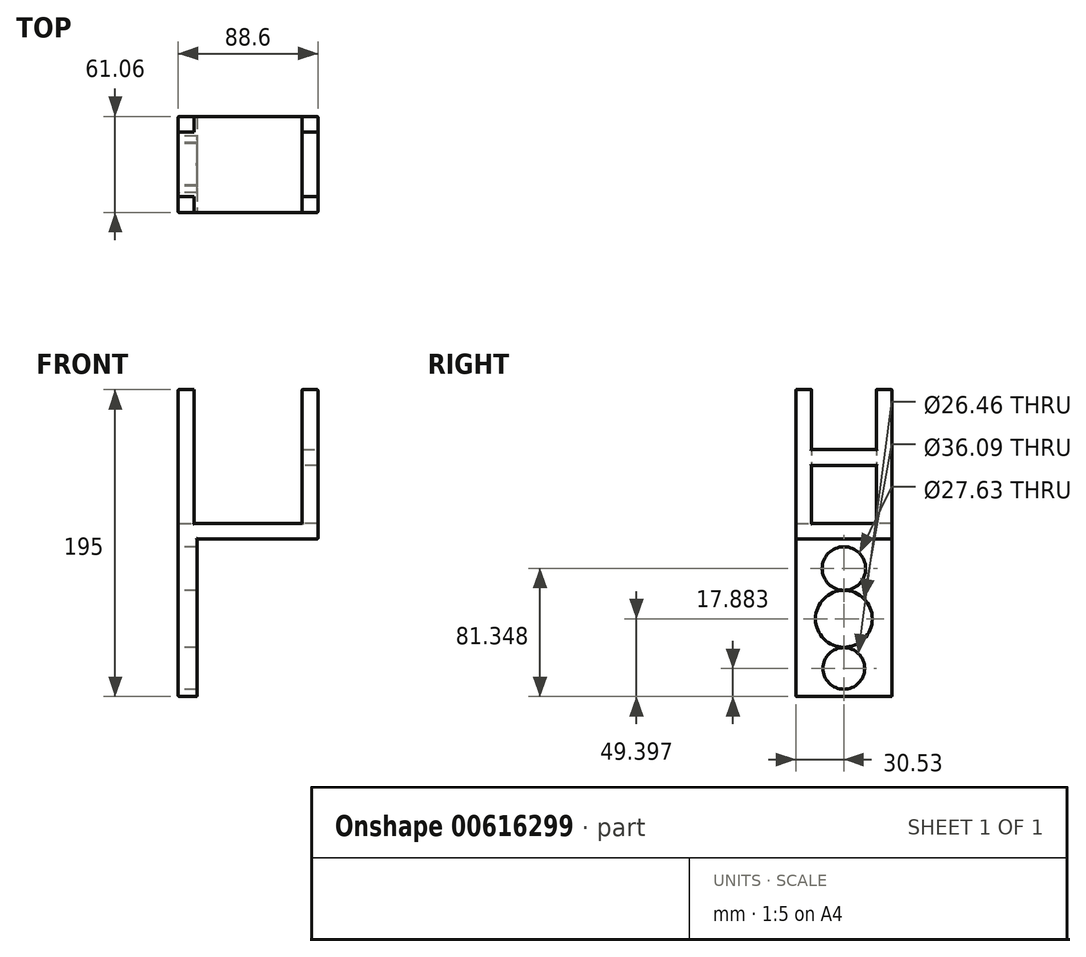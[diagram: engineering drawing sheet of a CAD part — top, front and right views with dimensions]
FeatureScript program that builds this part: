
annotation { "Feature Type Name" : "Feature", "Feature Type Description" : "" }
export const myFeature = defineFeature(function(context is Context, id is Id, definition is map)
    precondition{}
    {
        {
            var Q0;
            Q0=qCreatedBy(makeId("Top.planeOp"),FACE);
            var sketch = newSketch(context, id + "F0", { "sketchPlane" : qUnion([Q0])});
            skLineSegment(sketch, "E0.bottom", {"start": v(44.3, -30.53) * mm, "end": v(-44.3, -30.53) * mm});
            skLineSegment(sketch, "E0.top", {"start": v(44.3, 30.53) * mm, "end": v(-44.3, 30.53) * mm});
            skLineSegment(sketch, "E0.left", {"start": v(44.3, -30.53) * mm, "end": v(44.3, 30.53) * mm});
            skLineSegment(sketch, "E0.right", {"start": v(-44.3, -30.53) * mm, "end": v(-44.3, 30.53) * mm});
            skPoint(sketch, "E0.middle", {"position": v(0, 0) * mm});
            skSolve(sketch);
        }
        {
            var Q0;
            Q0=makeQuery(id+"F0.imprint","IMPRINT",FACE,{"disambiguationData":[TD([[makeQuery(id+"F0.imprint","IMPRINT",EDGE,{"derivedFrom":sQuery(id+"F0.wireOp",EDGE,"E0.bottom")}),-1.0]])]});
            extrude(context, id + "F1", {"entities" : qUnion([Q0]), "depth" : 10 * mm, "offsetDistance" : 25.4 * mm});
        }
        {
            var Q0;
            Q0=makeQuery(id+"F1.opExtrude","CAP_FACE",FACE,{"disambiguationData":[OSD([sQuery(id+"F0.wireOp",EDGE,"E0.bottom"),sQuery(id+"F0.wireOp",EDGE,"E0.top"),sQuery(id+"F0.wireOp",EDGE,"E0.left"),sQuery(id+"F0.wireOp",EDGE,"E0.right")])],"isStart":false});
            var sketch = newSketch(context, id + "F2", { "sketchPlane" : qUnion([Q0])});
            skLineSegment(sketch, "E1.bottom", {"start": v(-44.3, 30.53) * mm, "end": v(-34.3, 30.53) * mm});
            skLineSegment(sketch, "E1.top", {"start": v(-44.3, 20.53) * mm, "end": v(-34.3, 20.53) * mm});
            skLineSegment(sketch, "E1.left", {"start": v(-44.3, 30.53) * mm, "end": v(-44.3, 20.53) * mm});
            skLineSegment(sketch, "E1.right", {"start": v(-34.3, 30.53) * mm, "end": v(-34.3, 20.53) * mm});
            skLineSegment(sketch, "E2.bottom", {"start": v(44.3, 30.53) * mm, "end": v(34.3, 30.53) * mm});
            skLineSegment(sketch, "E2.top", {"start": v(44.3, 20.53) * mm, "end": v(34.3, 20.53) * mm});
            skLineSegment(sketch, "E2.left", {"start": v(44.3, 30.53) * mm, "end": v(44.3, 20.53) * mm});
            skLineSegment(sketch, "E2.right", {"start": v(34.3, 30.53) * mm, "end": v(34.3, 20.53) * mm});
            skLineSegment(sketch, "E3.bottom", {"start": v(44.3, -30.53) * mm, "end": v(34.3, -30.53) * mm});
            skLineSegment(sketch, "E3.top", {"start": v(44.3, -20.53) * mm, "end": v(34.3, -20.53) * mm});
            skLineSegment(sketch, "E3.left", {"start": v(44.3, -30.53) * mm, "end": v(44.3, -20.53) * mm});
            skLineSegment(sketch, "E3.right", {"start": v(34.3, -30.53) * mm, "end": v(34.3, -20.53) * mm});
            skLineSegment(sketch, "E4.bottom", {"start": v(-44.3, -30.53) * mm, "end": v(-34.3, -30.53) * mm});
            skLineSegment(sketch, "E4.top", {"start": v(-44.3, -20.53) * mm, "end": v(-34.3, -20.53) * mm});
            skLineSegment(sketch, "E4.left", {"start": v(-44.3, -30.53) * mm, "end": v(-44.3, -20.53) * mm});
            skLineSegment(sketch, "E4.right", {"start": v(-34.3, -30.53) * mm, "end": v(-34.3, -20.53) * mm});
            skSolve(sketch);
        }
        {
            var Q0;
            Q0=makeQuery(id+"F2.imprint","IMPRINT",FACE,{"disambiguationData":[TD([[makeQuery(id+"F2.imprint","IMPRINT",EDGE,{"derivedFrom":sQuery(id+"F2.wireOp",EDGE,"E1.bottom")}),1.0]])]});
            var Q1;
            Q1=makeQuery(id+"F2.imprint","IMPRINT",FACE,{"disambiguationData":[TD([[makeQuery(id+"F2.imprint","IMPRINT",EDGE,{"derivedFrom":sQuery(id+"F2.wireOp",EDGE,"E2.bottom")}),1.0]])]});
            var Q2;
            Q2=makeQuery(id+"F2.imprint","IMPRINT",FACE,{"disambiguationData":[TD([[makeQuery(id+"F2.imprint","IMPRINT",EDGE,{"derivedFrom":sQuery(id+"F2.wireOp",EDGE,"E3.bottom")}),-1.0]])]});
            var Q3;
            Q3=makeQuery(id+"F2.imprint","IMPRINT",FACE,{"disambiguationData":[TD([[makeQuery(id+"F2.imprint","IMPRINT",EDGE,{"derivedFrom":sQuery(id+"F2.wireOp",EDGE,"E4.bottom")}),-1.0]])]});
            extrude(context, id + "F3", {"entities" : qUnion([Q0, Q1, Q2, Q3]), "operationType" : NewBodyOperationType.ADD, "depth" : 85 * mm, "offsetDistance" : 25 * mm});
        }
        {
            var Q0;
            Q0=makeQuery(id+"F1.opExtrude","CAP_FACE",FACE,{"disambiguationData":[OSD([sQuery(id+"F0.wireOp",EDGE,"E0.bottom"),sQuery(id+"F0.wireOp",EDGE,"E0.top"),sQuery(id+"F0.wireOp",EDGE,"E0.left"),sQuery(id+"F0.wireOp",EDGE,"E0.right")])],"isStart":true});
            var sketch = newSketch(context, id + "F4", { "sketchPlane" : qUnion([Q0])});
            skLineSegment(sketch, "E5.bottom", {"start": v(-44.3, -30.53) * mm, "end": v(-32.3, -30.53) * mm});
            skLineSegment(sketch, "E5.top", {"start": v(-44.3, 30.53) * mm, "end": v(-32.3, 30.53) * mm});
            skLineSegment(sketch, "E5.left", {"start": v(-44.3, -30.53) * mm, "end": v(-44.3, 30.53) * mm});
            skLineSegment(sketch, "E5.right", {"start": v(-32.3, -30.53) * mm, "end": v(-32.3, 30.53) * mm});
            skSolve(sketch);
        }
        {
            var Q0;
            Q0=makeQuery(id+"F4.imprint","IMPRINT",FACE,{"disambiguationData":[TD([[makeQuery(id+"F4.imprint","IMPRINT",EDGE,{"derivedFrom":sQuery(id+"F4.wireOp",EDGE,"E5.bottom")}),-1.0]])]});
            extrude(context, id + "F5", {"entities" : qUnion([Q0]), "operationType" : NewBodyOperationType.ADD, "depth" : 50 * mm, "offsetDistance" : 25 * mm});
        }
        {
            var Q0;
            Q0=makeQuery(id+"F5.opExtrude","CAP_FACE",FACE,{"disambiguationData":[OSD([sQuery(id+"F4.wireOp",EDGE,"E5.bottom"),sQuery(id+"F4.wireOp",EDGE,"E5.top"),sQuery(id+"F4.wireOp",EDGE,"E5.left"),sQuery(id+"F4.wireOp",EDGE,"E5.right")])],"isStart":false});
            extrude(context, id + "F6", {"entities" : qUnion([Q0]), "operationType" : NewBodyOperationType.ADD, "depth" : 50 * mm, "offsetDistance" : 25 * mm});
        }
        {
            var Q0;
            Q0=makeQuery(id+"F3.opExtrude","SWEPT_FACE",FACE,{"disambiguationData":[OSD([sQuery(id+"F2.wireOp",EDGE,"E2.top")])]});
            var sketch = newSketch(context, id + "F7", { "sketchPlane" : qUnion([Q0])});
            skLineSegment(sketch, "E6.bottom", {"start": v(34.3, 46.8) * mm, "end": v(44.3, 46.8) * mm});
            skLineSegment(sketch, "E6.top", {"start": v(34.3, 56.89) * mm, "end": v(44.3, 56.89) * mm});
            skLineSegment(sketch, "E6.left", {"start": v(34.3, 46.8) * mm, "end": v(34.3, 56.89) * mm});
            skLineSegment(sketch, "E6.right", {"start": v(44.3, 46.8) * mm, "end": v(44.3, 56.89) * mm});
            skSolve(sketch);
        }
        {
            var Q0;
            Q0=makeQuery(id+"F7.imprint","IMPRINT",FACE,{"disambiguationData":[TD([[makeQuery(id+"F7.imprint","IMPRINT",EDGE,{"derivedFrom":sQuery(id+"F7.wireOp",EDGE,"E6.bottom")}),1.0]])]});
            extrude(context, id + "F8", {"entities" : qUnion([Q0]), "operationType" : NewBodyOperationType.ADD, "depth" : 42 * mm, "offsetDistance" : 25 * mm});
        }
        {
            var Q0;
            {var subQ0=sQuery(id+"F4.wireOp",EDGE,"E5.left");Q0=makeQuery(id+"F6.boolean.opBoolean","MERGE",FACE,{"derivedFrom":[makeQuery(id+"F5.boolean.opBoolean","MERGE",FACE,{"derivedFrom":[makeQuery(id+"F3.boolean.opBoolean","MERGE",FACE,{"derivedFrom":[makeQuery(id+"F1.opExtrude","SWEPT_FACE",FACE,{"disambiguationData":[OSD([sQuery(id+"F0.wireOp",EDGE,"E0.right")])]}),makeQuery(id+"F3.opExtrude","SWEPT_FACE",FACE,{"disambiguationData":[OSD([sQuery(id+"F2.wireOp",EDGE,"E1.left")])]}),makeQuery(id+"F3.opExtrude","SWEPT_FACE",FACE,{"disambiguationData":[OSD([sQuery(id+"F2.wireOp",EDGE,"E4.left")])]})]}),makeQuery(id+"F5.opExtrude","SWEPT_FACE",FACE,{"disambiguationData":[OSD([subQ0])]})]}),makeQuery(id+"F6.opExtrude","SWEPT_FACE",FACE,{"disambiguationData":[OSD([subQ0])]})]});}
            var sketch = newSketch(context, id + "F9", { "sketchPlane" : qUnion([Q0])});
            skCircle(sketch, "E7", {"center": v(0, -50.6) * mm, "radius": 18.04 * mm});
            skCircle(sketch, "E8", {"center": v(0, -18.65) * mm, "radius": 13.82 * mm});
            skSolve(sketch);
        }
        {
            var Q0;
            Q0=makeQuery(id+"F9.imprint","IMPRINT",FACE,{"disambiguationData":[TD([[makeQuery(id+"F9.imprint","IMPRINT",EDGE,{"derivedFrom":sQuery(id+"F9.wireOp",EDGE,"E7")}),-1.0]])]});
            var sketch = newSketch(context, id + "F10", { "sketchPlane" : qUnion([Q0])});
            skCircle(sketch, "E9", {"center": v(0, -82.12) * mm, "radius": 13.23 * mm});
            skSolve(sketch);
        }
        {
            var Q0;
            Q0=makeQuery(id+"F10.imprint","IMPRINT",FACE,{"disambiguationData":[TD([[makeQuery(id+"F10.imprint","IMPRINT",EDGE,{"derivedFrom":sQuery(id+"F10.wireOp",EDGE,"E9")}),1.0]])]});
            extrude(context, id + "F11", {"entities" : qUnion([Q0]), "operationType" : NewBodyOperationType.REMOVE, "oppositeDirection" : true, "depth" : 25 * mm, "offsetDistance" : 25 * mm});
        }
        {
            var Q0;
            Q0=makeQuery(id+"F9.imprint","IMPRINT",FACE,{"disambiguationData":[TD([[makeQuery(id+"F9.imprint","IMPRINT",EDGE,{"derivedFrom":sQuery(id+"F9.wireOp",EDGE,"E8")}),1.0]])]});
            var Q1;
            Q1=makeQuery(id+"F9.imprint","IMPRINT",FACE,{"disambiguationData":[TD([[makeQuery(id+"F9.imprint","IMPRINT",EDGE,{"derivedFrom":sQuery(id+"F9.wireOp",EDGE,"E7")}),1.0]])]});
            extrude(context, id + "F12", {"entities" : qUnion([Q0, Q1]), "operationType" : NewBodyOperationType.REMOVE, "oppositeDirection" : true, "depth" : 25 * mm, "offsetDistance" : 25 * mm});
        }
        {
            var Q0;
            {var subQ0=sQuery(id+"F4.wireOp",EDGE,"E5.bottom");Q0=makeQuery(id+"F6.boolean.opBoolean","MERGE",FACE,{"derivedFrom":[makeQuery(id+"F5.boolean.opBoolean","MERGE",FACE,{"derivedFrom":[makeQuery(id+"F3.boolean.opBoolean","MERGE",FACE,{"derivedFrom":[makeQuery(id+"F1.opExtrude","SWEPT_FACE",FACE,{"disambiguationData":[OSD([sQuery(id+"F0.wireOp",EDGE,"E0.top")])]}),makeQuery(id+"F3.opExtrude","SWEPT_FACE",FACE,{"disambiguationData":[OSD([sQuery(id+"F2.wireOp",EDGE,"E1.bottom")])]}),makeQuery(id+"F3.opExtrude","SWEPT_FACE",FACE,{"disambiguationData":[OSD([sQuery(id+"F2.wireOp",EDGE,"E2.bottom")])]})]}),makeQuery(id+"F5.opExtrude","SWEPT_FACE",FACE,{"disambiguationData":[OSD([subQ0])]})]}),makeQuery(id+"F6.opExtrude","SWEPT_FACE",FACE,{"disambiguationData":[OSD([subQ0])]})]});}
            fillet(context, id + "F13", {"entities" : qUnion([Q0]), "radius" : 0.5 * mm, "tangentPropagation" : true, "allowEdgeOverflow" : false});
        }
        {
            var Q0;
            {var subQ0=sQuery(id+"F4.wireOp",EDGE,"E5.left");Q0=makeQuery(id+"F6.boolean.opBoolean","MERGE",FACE,{"derivedFrom":[makeQuery(id+"F5.boolean.opBoolean","MERGE",FACE,{"derivedFrom":[makeQuery(id+"F3.boolean.opBoolean","MERGE",FACE,{"derivedFrom":[makeQuery(id+"F1.opExtrude","SWEPT_FACE",FACE,{"disambiguationData":[OSD([sQuery(id+"F0.wireOp",EDGE,"E0.right")])]}),makeQuery(id+"F3.opExtrude","SWEPT_FACE",FACE,{"disambiguationData":[OSD([sQuery(id+"F2.wireOp",EDGE,"E1.left")])]}),makeQuery(id+"F3.opExtrude","SWEPT_FACE",FACE,{"disambiguationData":[OSD([sQuery(id+"F2.wireOp",EDGE,"E4.left")])]})]}),makeQuery(id+"F5.opExtrude","SWEPT_FACE",FACE,{"disambiguationData":[OSD([subQ0])]})]}),makeQuery(id+"F6.opExtrude","SWEPT_FACE",FACE,{"disambiguationData":[OSD([subQ0])]})]});}
            var Q1;
            Q1=makeQuery(id+"F8.boolean.opBoolean","MERGE",FACE,{"derivedFrom":[makeQuery(id+"F3.opExtrude","SWEPT_FACE",FACE,{"disambiguationData":[OSD([sQuery(id+"F2.wireOp",EDGE,"E2.right")])]}),makeQuery(id+"F3.opExtrude","SWEPT_FACE",FACE,{"disambiguationData":[OSD([sQuery(id+"F2.wireOp",EDGE,"E3.right")])]}),makeQuery(id+"F8.opExtrude","SWEPT_FACE",FACE,{"disambiguationData":[OSD([sQuery(id+"F7.wireOp",EDGE,"E6.left")])]})]});
            fillet(context, id + "F14", {"entities" : qUnion([Q0, Q1]), "radius" : 0.5 * mm, "tangentPropagation" : true, "allowEdgeOverflow" : false});
        }
        {
            var Q0;
            {var subQ0=sQuery(id+"F4.wireOp",EDGE,"E5.top");Q0=makeQuery(id+"F6.boolean.opBoolean","MERGE",FACE,{"derivedFrom":[makeQuery(id+"F5.boolean.opBoolean","MERGE",FACE,{"derivedFrom":[makeQuery(id+"F3.boolean.opBoolean","MERGE",FACE,{"derivedFrom":[makeQuery(id+"F1.opExtrude","SWEPT_FACE",FACE,{"disambiguationData":[OSD([sQuery(id+"F0.wireOp",EDGE,"E0.bottom")])]}),makeQuery(id+"F3.opExtrude","SWEPT_FACE",FACE,{"disambiguationData":[OSD([sQuery(id+"F2.wireOp",EDGE,"E3.bottom")])]}),makeQuery(id+"F3.opExtrude","SWEPT_FACE",FACE,{"disambiguationData":[OSD([sQuery(id+"F2.wireOp",EDGE,"E4.bottom")])]})]}),makeQuery(id+"F5.opExtrude","SWEPT_FACE",FACE,{"disambiguationData":[OSD([subQ0])]})]}),makeQuery(id+"F6.opExtrude","SWEPT_FACE",FACE,{"disambiguationData":[OSD([subQ0])]})]});}
            var Q1;
            {var subQ0=sQuery(id+"F4.wireOp",EDGE,"E5.bottom");Q1=makeQuery(id+"F6.boolean.opBoolean","MERGE",FACE,{"derivedFrom":[makeQuery(id+"F5.boolean.opBoolean","MERGE",FACE,{"derivedFrom":[makeQuery(id+"F3.boolean.opBoolean","MERGE",FACE,{"derivedFrom":[makeQuery(id+"F1.opExtrude","SWEPT_FACE",FACE,{"disambiguationData":[OSD([sQuery(id+"F0.wireOp",EDGE,"E0.top")])]}),makeQuery(id+"F3.opExtrude","SWEPT_FACE",FACE,{"disambiguationData":[OSD([sQuery(id+"F2.wireOp",EDGE,"E1.bottom")])]}),makeQuery(id+"F3.opExtrude","SWEPT_FACE",FACE,{"disambiguationData":[OSD([sQuery(id+"F2.wireOp",EDGE,"E2.bottom")])]})]}),makeQuery(id+"F5.opExtrude","SWEPT_FACE",FACE,{"disambiguationData":[OSD([subQ0])]})]}),makeQuery(id+"F6.opExtrude","SWEPT_FACE",FACE,{"disambiguationData":[OSD([subQ0])]})]});}
            fillet(context, id + "F15", {"entities" : qUnion([Q0, Q1]), "radius" : 0.5 * mm, "tangentPropagation" : true, "allowEdgeOverflow" : false});
        }
        {
            var Q0;
            Q0=makeQuery(id+"F8.boolean.opBoolean","MERGE",FACE,{"derivedFrom":[makeQuery(id+"F3.boolean.opBoolean","MERGE",FACE,{"derivedFrom":[makeQuery(id+"F1.opExtrude","SWEPT_FACE",FACE,{"disambiguationData":[OSD([sQuery(id+"F0.wireOp",EDGE,"E0.left")])]}),makeQuery(id+"F3.opExtrude","SWEPT_FACE",FACE,{"disambiguationData":[OSD([sQuery(id+"F2.wireOp",EDGE,"E2.left")])]}),makeQuery(id+"F3.opExtrude","SWEPT_FACE",FACE,{"disambiguationData":[OSD([sQuery(id+"F2.wireOp",EDGE,"E3.left")])]})]}),makeQuery(id+"F8.opExtrude","SWEPT_FACE",FACE,{"disambiguationData":[OSD([sQuery(id+"F7.wireOp",EDGE,"E6.right")])]})]});
            var Q1;
            {var subQ0=sQuery(id+"F4.wireOp",EDGE,"E5.right");Q1=makeQuery(id+"F6.boolean.opBoolean","MERGE",FACE,{"derivedFrom":[makeQuery(id+"F5.opExtrude","SWEPT_FACE",FACE,{"disambiguationData":[OSD([subQ0])]}),makeQuery(id+"F6.opExtrude","SWEPT_FACE",FACE,{"disambiguationData":[OSD([subQ0])]})]});}
            fillet(context, id + "F16", {"entities" : qUnion([Q0, Q1]), "radius" : 0.5 * mm, "tangentPropagation" : true, "allowEdgeOverflow" : false});
        }
    });
